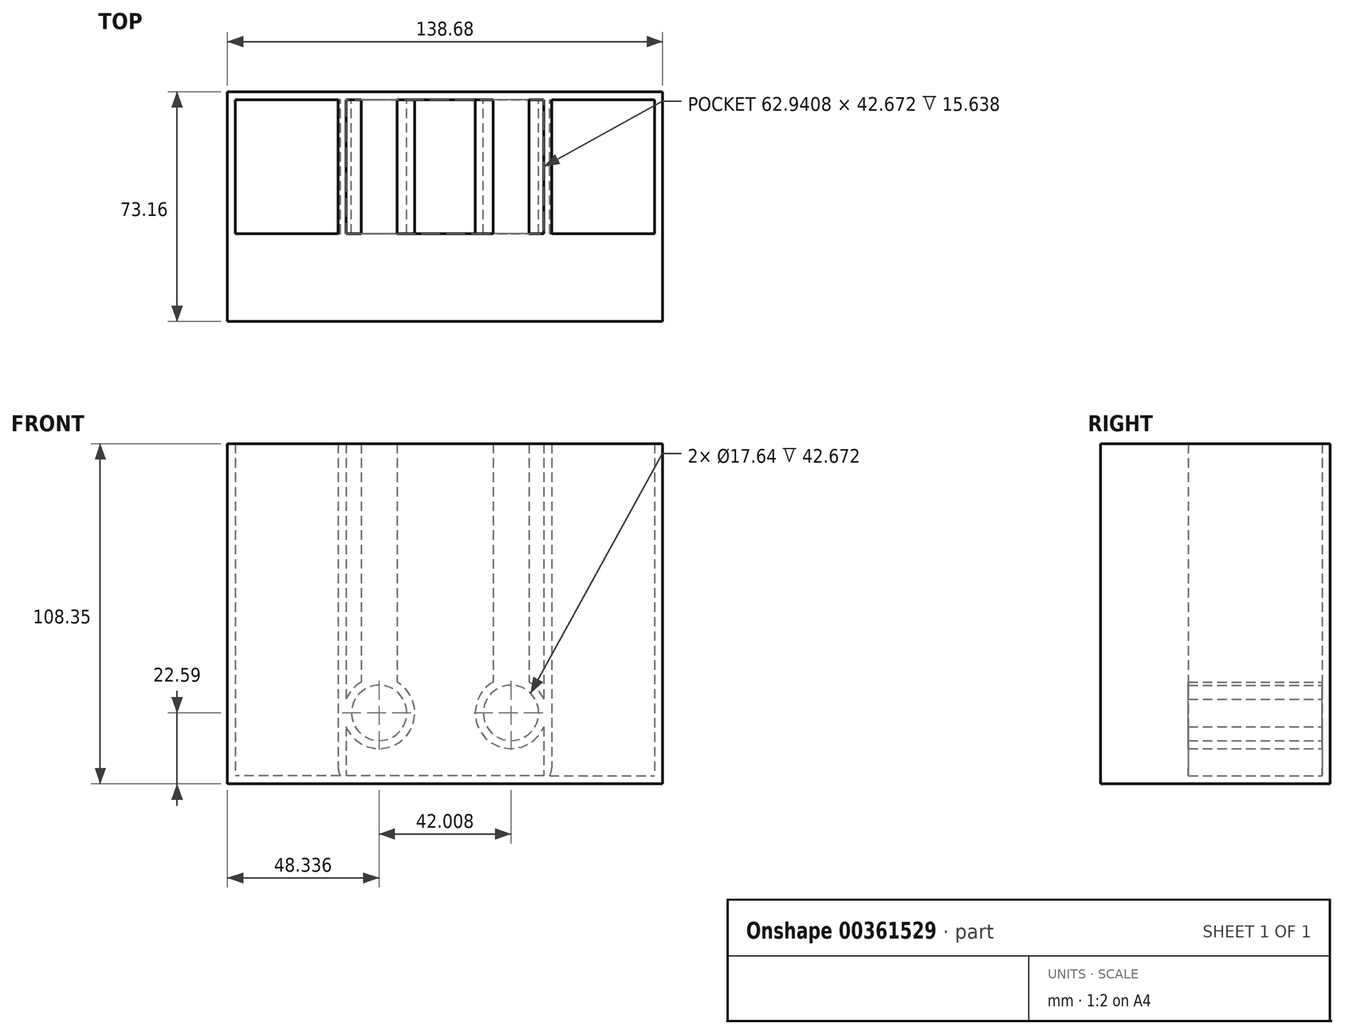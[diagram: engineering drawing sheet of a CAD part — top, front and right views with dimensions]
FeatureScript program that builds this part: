
annotation { "Feature Type Name" : "Feature", "Feature Type Description" : "" }
export const myFeature = defineFeature(function(context is Context, id is Id, definition is map)
    precondition{}
    {
        {
            var Q0;
            Q0=qCreatedBy(makeId("Front.planeOp"),FACE);
            var sketch = newSketch(context, id + "F0", { "sketchPlane" : qUnion([Q0])});
            skLineSegment(sketch, "E0.bottom", {"start": v(34.01, 9.82) * mm, "end": v(-69.34, 9.82) * mm});
            skLineSegment(sketch, "E0.top", {"start": v(34.01, -22.6) * mm, "end": v(-69.34, -22.6) * mm});
            skLineSegment(sketch, "E0.left", {"start": v(34.01, 9.82) * mm, "end": v(34.01, -22.6) * mm});
            skLineSegment(sketch, "E0.right", {"start": v(-69.34, 9.82) * mm, "end": v(-69.34, -22.6) * mm});
            skCircle(sketch, "E1", {"center": v(-21, 0) * mm, "radius": 8.82 * mm});
            skSolve(sketch);
        }
        {
            var Q0;
            Q0=sQuery(id+"F0.wireOp",EDGE,"E1");
            extrude(context, id + "F1", {"bodyType" : ToolBodyType.SURFACE, "surfaceEntities" : qUnion([Q0]), "endBound" : BoundingType.SYMMETRIC, "depth" : 68.58 * mm});
        }
        {
            var Q0;
            Q0=makeQuery(id+"F0.imprint","IMPRINT",FACE,{"disambiguationData":[TD([[makeQuery(id+"F0.imprint","IMPRINT",EDGE,{"derivedFrom":sQuery(id+"F0.wireOp",EDGE,"E0.bottom")}),1.0]])]});
            extrude(context, id + "F2", {"entities" : qUnion([Q0]), "endBound" : BoundingType.SYMMETRIC, "depth" : 47.75 * mm});
        }
        {
            var Q0;
            Q0=makeQuery(id+"F2.opExtrude","SWEPT_FACE",FACE,{"disambiguationData":[OSD([sQuery(id+"F0.wireOp",EDGE,"E0.bottom")])]});
            shell(context, id + "F3", {"entities" : qUnion([Q0]), "thickness" : 2.54 * mm});
        }
        {
            var Q0;
            Q0=makeQuery(id+"F2.opExtrude","SWEPT_EDGE",EDGE,{"disambiguationData":[OSD([sQuery(id+"F0.wireOp",EDGE,"E0.top"),sQuery(id+"F0.wireOp",EDGE,"E0.left")])]});
            fillet(context, id + "F4", {"entities" : qUnion([Q0]), "radius" : 5.08 * mm, "tangentPropagation" : true, "allowEdgeOverflow" : false});
        }
        {
            var Q0;
            Q0=makeQuery(id+"F2.opExtrude","SWEPT_FACE",FACE,{"disambiguationData":[OSD([sQuery(id+"F0.wireOp",EDGE,"E0.bottom")])]});
            extrude(context, id + "F5", {"entities" : qUnion([Q0]), "operationType" : NewBodyOperationType.ADD, "depth" : 75.95 * mm});
        }
        {
            var Q0;
            {var subQ0=sQuery(id+"F0.wireOp",EDGE,"E0.bottom");Q0=makeQuery(id+"F5.boolean.opBoolean","MERGE",FACE,{"derivedFrom":[makeQuery(id+"F2.opExtrude","CAP_FACE",FACE,{"disambiguationData":[OSD([subQ0,sQuery(id+"F0.wireOp",EDGE,"E0.top"),sQuery(id+"F0.wireOp",EDGE,"E0.left"),sQuery(id+"F0.wireOp",EDGE,"E0.right"),sQuery(id+"F0.wireOp",EDGE,"E1")])],"isStart":false}),makeQuery(id+"F5.opExtrude","SWEPT_FACE",FACE,{"disambiguationData":[OSD([subQ0]),TDD([makeQuery(id+"F2.opExtrude","CAP_EDGE",EDGE,{"disambiguationData":[OSD([subQ0])],"isStart":false})])]})]});}
            extrude(context, id + "F6", {"entities" : qUnion([Q0]), "operationType" : NewBodyOperationType.ADD, "depth" : 25.4 * mm});
        }
        {
            var Q0;
            Q0=makeQuery(id+"F2.opExtrude","SWEPT_BODY",BODY,{"disambiguationData":[OSD([sQuery(id+"F0.wireOp",EDGE,"E0.bottom"),sQuery(id+"F0.wireOp",EDGE,"E0.top"),sQuery(id+"F0.wireOp",EDGE,"E0.left"),sQuery(id+"F0.wireOp",EDGE,"E0.right"),sQuery(id+"F0.wireOp",EDGE,"E1")])]});
            var Q1;
            Q1=qCreatedBy(makeId("Right.planeOp"),FACE);
            mirror(context, id + "F7", {"operationType" : NewBodyOperationType.ADD, "entities" : qUnion([Q0]), "mirrorPlane" : qUnion([Q1])});
        }
    });
